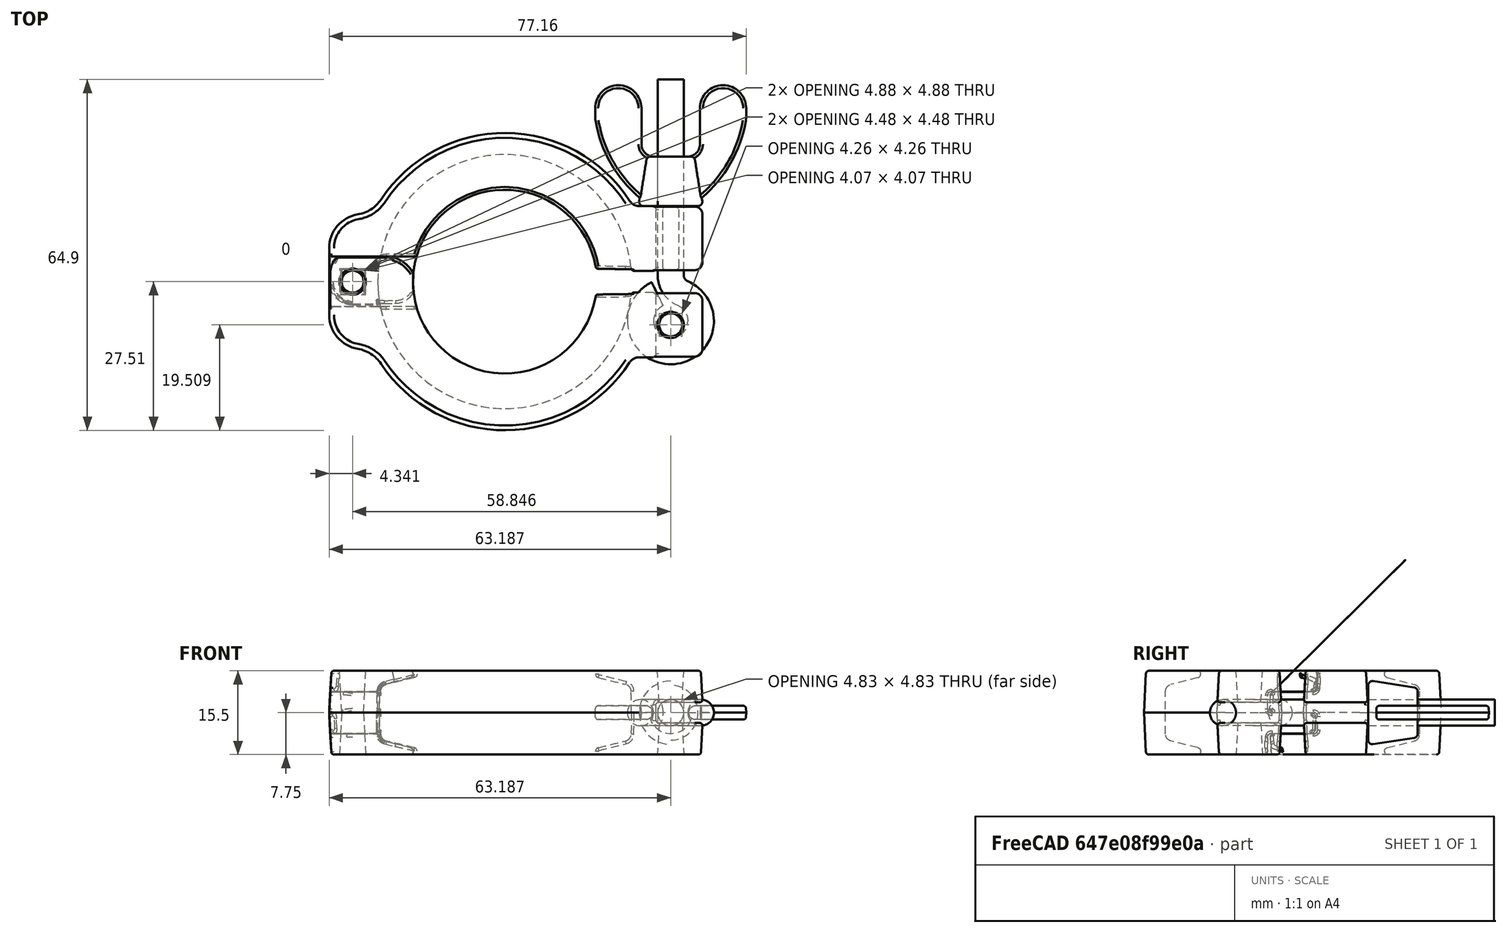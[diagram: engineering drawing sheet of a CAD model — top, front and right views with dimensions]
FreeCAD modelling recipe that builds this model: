
FCSTD DOCUMENT  (FreeCAD 0.17R11834 (Git))
Label: clamp
License: All rights reserved
LicenseURL: http://en.wikipedia.org/wiki/All_rights_reserved
objects: Part::Feature×3, App::Part×1, Part::Compound×1
note: 4 computed .brp shape members not serialized (recipe doc carries the construction recipe); baked Part::Feature solids carry a one-line shape summary decoded from their .brp

FEATURE [Part::Feature] Part__Feature  label="clamp"
  shape: bbox 69.13 x 44.65 x 15.56 mm, 163 faces (baked)
FEATURE [Part::Feature] Part__Feature001  label="clamp001"
  shape: bbox 71.87 x 56.03 x 15.56 mm, 176 faces (baked)
FEATURE [Part::Feature] Part__Feature002  label="clamp002"
  shape: bbox 27.94 x 26.64 x 13.06 mm, 63 faces (baked)
FEATURE [App::Part] clamp  label="clamp003"
  Group = -> [Part__Feature,Part__Feature001,Part__Feature002]
  License = CC BY 3.0
  LicenseURL = http://creativecommons.org/licenses/by/3.0/
  Origin = -> Origin
FEATURE [Part::Compound] Compound
  Links = -> [Part__Feature,Part__Feature001,Part__Feature002]
